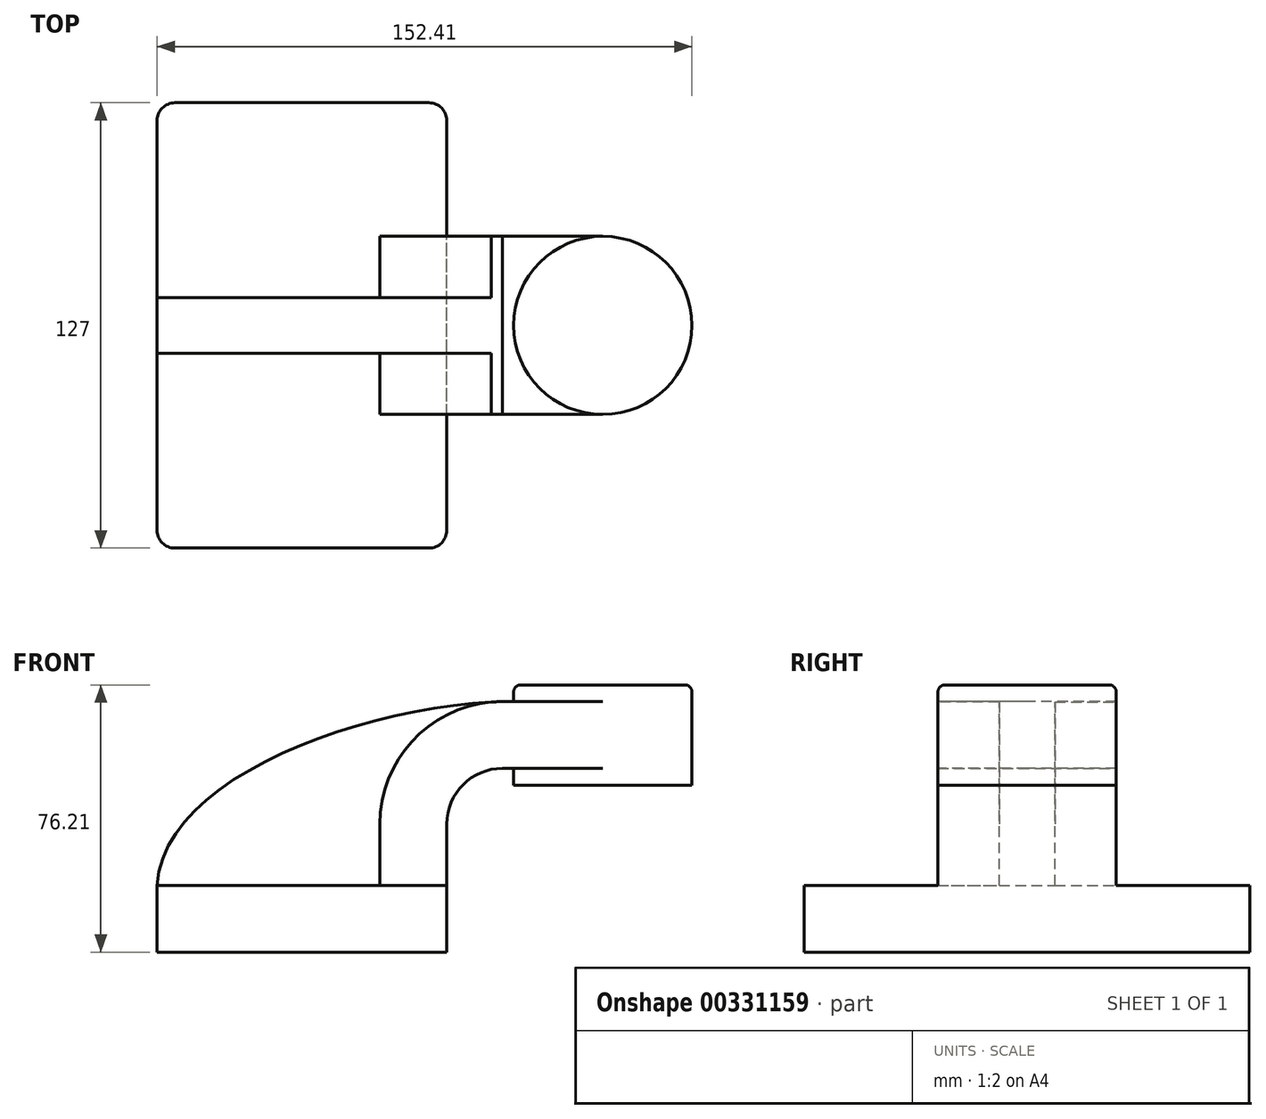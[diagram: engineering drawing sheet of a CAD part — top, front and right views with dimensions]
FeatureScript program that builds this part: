
annotation { "Feature Type Name" : "Feature", "Feature Type Description" : "" }
export const myFeature = defineFeature(function(context is Context, id is Id, definition is map)
    precondition{}
    {
        {
            var Q0;
            Q0=qCreatedBy(makeId("Front.planeOp"),FACE);
            var sketch = newSketch(context, id + "F0", { "sketchPlane" : qUnion([Q0])});
            skLineSegment(sketch, "E0.rect.bottom", {"start": v(-41.28, 9.52) * mm, "end": v(41.28, 9.52) * mm});
            skLineSegment(sketch, "E0.rect.top", {"start": v(-41.28, -9.52) * mm, "end": v(41.28, -9.52) * mm});
            skLineSegment(sketch, "E0.rect.left", {"start": v(-41.28, 9.52) * mm, "end": v(-41.28, -9.52) * mm});
            skLineSegment(sketch, "E0.rect.right", {"start": v(41.28, 9.52) * mm, "end": v(41.28, -9.52) * mm});
            skPoint(sketch, "E0.rect.middle", {"position": v(0, 0) * mm});
            skLineSegment(sketch, "E1", {"start": v(41.28, 9.52) * mm, "end": v(41.28, 27) * mm});
            skArc(sketch, "E2", {"start": v(41.28, 27) * mm, "mid": v(45.92, 38.23) * mm, "end": v(57.15, 42.88) * mm});
            skLineSegment(sketch, "E3", {"start": v(57.15, 42.88) * mm, "end": v(85.72, 42.88) * mm});
            skLineSegment(sketch, "E4.rect.bottom", {"start": v(60.32, 38.1) * mm, "end": v(111.12, 38.1) * mm});
            skLineSegment(sketch, "E4.rect.top", {"start": v(60.32, 66.68) * mm, "end": v(111.12, 66.68) * mm});
            skLineSegment(sketch, "E4.rect.left", {"start": v(60.32, 38.1) * mm, "end": v(60.32, 66.68) * mm});
            skLineSegment(sketch, "E4.rect.right", {"start": v(111.13, 38.1) * mm, "end": v(111.12, 66.68) * mm});
            skPoint(sketch, "E4.rect.middle", {"position": v(85.72, 52.39) * mm});
            skLineSegment(sketch, "E5.0", {"start": v(57.15, 61.93) * mm, "end": v(85.72, 61.93) * mm});
            skArc(sketch, "E5.1", {"start": v(22.23, 27) * mm, "mid": v(32.45, 51.7) * mm, "end": v(57.15, 61.93) * mm});
            skLineSegment(sketch, "E5.2", {"start": v(22.23, 9.52) * mm, "end": v(22.23, 27) * mm});
            skLineSegment(sketch, "E6", {"start": v(85.72, 38.1) * mm, "end": v(85.72, 66.68) * mm});
            skFitSpline(sketch, "E7", {"points": [v(-41.28, 9.53) * mm, v(57.15, 61.93) * mm], "startDerivative": vector(5.2, 92.34) * mm, "endDerivative": vector(120.92, 4.22) * mm});
            skSolve(sketch);
        }
        {
            var Q0;
            Q0=makeQuery(id+"F0.imprint","IMPRINT",FACE,{"disambiguationData":[TD([[makeQuery(id+"F0.imprint","IMPRINT",EDGE,{"derivedFrom":sQuery(id+"F0.wireOp",EDGE,"E0.rect.top")}),1.0]])]});
            extrude(context, id + "F1", {"entities" : qUnion([Q0]), "endBound" : BoundingType.SYMMETRIC, "depth" : 127 * mm});
        }
        {
            var Q0;
            {var subQ9=sQuery(id+"F0.wireOp",EDGE,"E1");Q0=makeQuery(id+"F0.imprint","IMPRINT",FACE,{"disambiguationData":[TD([[makeQuery(id+"F0.imprint","IMPRINT",EDGE,{"derivedFrom":subQ9}),1.0]])]});}
            var Q1;
            {var subQ0=sQuery(id+"F0.wireOp",EDGE,"E6");var subQ1=sQuery(id+"F0.wireOp",EDGE,"E3");var subQ2=makeQuery(id+"F0.imprint","INTERSECT",VERTEX,{"derivedFrom":[subQ1,subQ0]});Q1=makeQuery(id+"F0.imprint","IMPRINT",FACE,{"disambiguationData":[TD([[makeQuery(id+"F0.imprint","IMPRINT",EDGE,{"disambiguationData":[TD([[subQ2,1.0]])],"derivedFrom":subQ1}),1.0]])]});}
            extrude(context, id + "F2", {"entities" : qUnion([Q0, Q1]), "operationType" : NewBodyOperationType.ADD, "endBound" : BoundingType.SYMMETRIC, "depth" : 50.8 * mm});
        }
        {
            var Q0;
            {var subQ3=sQuery(id+"F0.wireOp",EDGE,"E5.2");Q0=makeQuery(id+"F0.imprint","IMPRINT",FACE,{"disambiguationData":[TD([[makeQuery(id+"F0.imprint","IMPRINT",EDGE,{"derivedFrom":subQ3}),1.0]])]});}
            extrude(context, id + "F3", {"entities" : qUnion([Q0]), "operationType" : NewBodyOperationType.ADD, "endBound" : BoundingType.SYMMETRIC, "depth" : 15.88 * mm});
        }
        {
            var Q0;
            {var subQ5=sQuery(id+"F0.wireOp",EDGE,"E4.rect.right");Q0=makeQuery(id+"F0.imprint","IMPRINT",FACE,{"disambiguationData":[TD([[makeQuery(id+"F0.imprint","IMPRINT",EDGE,{"derivedFrom":subQ5}),1.0]])]});}
            var Q1;
            Q1=sQuery(id+"F0.wireOp",EDGE,"E6");
            revolve(context, id + "F4", {"operationType" : NewBodyOperationType.ADD, "entities" : qUnion([Q0]), "axis" : qUnion([Q1]), "revolveType" : RevolveType.FULL});
        }
        {
            var Q0;
            Q0=makeQuery(id+"F1.opExtrude","CAP_EDGE",EDGE,{"disambiguationData":[OSD([sQuery(id+"F0.wireOp",EDGE,"E0.rect.right")])],"isStart":false});
            var Q1;
            Q1=makeQuery(id+"F1.opExtrude","CAP_EDGE",EDGE,{"disambiguationData":[OSD([sQuery(id+"F0.wireOp",EDGE,"E0.rect.left")])],"isStart":false});
            var Q2;
            Q2=makeQuery(id+"F1.opExtrude","CAP_EDGE",EDGE,{"disambiguationData":[OSD([sQuery(id+"F0.wireOp",EDGE,"E0.rect.right")])],"isStart":true});
            var Q3;
            Q3=makeQuery(id+"F1.opExtrude","CAP_EDGE",EDGE,{"disambiguationData":[OSD([sQuery(id+"F0.wireOp",EDGE,"E0.rect.left")])],"isStart":true});
            fillet(context, id + "F5", {"entities" : qUnion([Q0, Q1, Q2, Q3]), "radius" : 5.08 * mm, "tangentPropagation" : true, "allowEdgeOverflow" : false});
        }
        {
            var Q0;
            Q0=makeQuery(id+"F4.opRevolve","SWEPT_EDGE",EDGE,{"disambiguationData":[OSD([sQuery(id+"F0.wireOp",EDGE,"E4.rect.top"),sQuery(id+"F0.wireOp",EDGE,"E4.rect.right")])]});
            fillet(context, id + "F6", {"entities" : qUnion([Q0]), "radius" : 2.03 * mm, "tangentPropagation" : true, "allowEdgeOverflow" : false});
        }
    });
